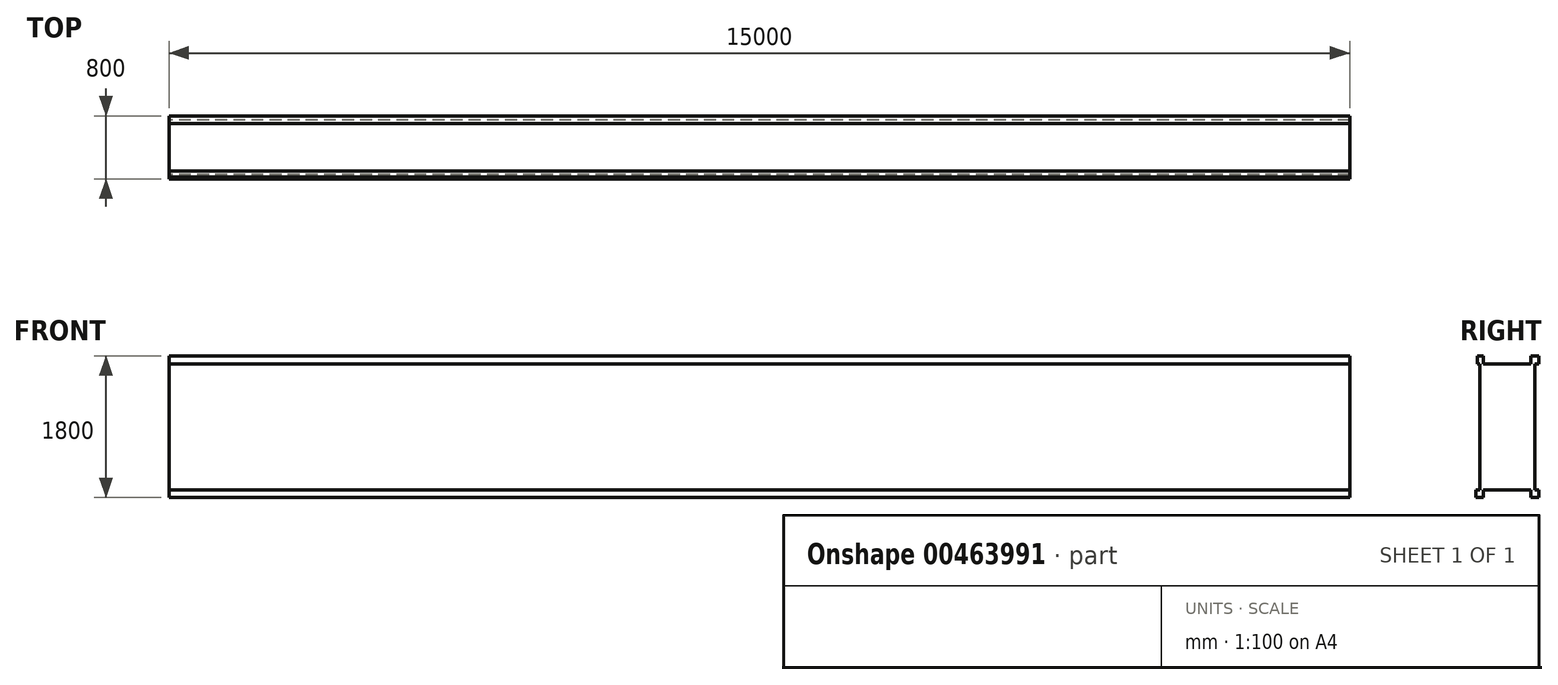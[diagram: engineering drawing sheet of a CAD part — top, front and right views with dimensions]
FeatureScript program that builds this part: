
annotation { "Feature Type Name" : "Feature", "Feature Type Description" : "" }
export const myFeature = defineFeature(function(context is Context, id is Id, definition is map)
    precondition{}
    {
        {
            var Q0;
            Q0=qCreatedBy(makeId("Right.planeOp"),FACE);
            var sketch = newSketch(context, id + "F0", { "sketchPlane" : qUnion([Q0])});
            skLineSegment(sketch, "E0", {"start": v(0, 0) * mm, "end": v(-100, 0) * mm});
            skLineSegment(sketch, "E1", {"start": v(-100, 0) * mm, "end": v(-100, 100) * mm});
            skLineSegment(sketch, "E2", {"start": v(-100, 100) * mm, "end": v(-700, 100) * mm});
            skLineSegment(sketch, "E3", {"start": v(-700, 100) * mm, "end": v(-700, 0) * mm});
            skLineSegment(sketch, "E4", {"start": v(-700, 0) * mm, "end": v(-800, 0) * mm});
            skPoint(sketch, "E5.endSnap0", {"position": v(-750, 0) * mm});
            skLineSegment(sketch, "E6", {"start": v(0, 0) * mm, "end": v(0, 100) * mm});
            skLineSegment(sketch, "E7", {"start": v(0, 100) * mm, "end": v(-50, 100) * mm});
            skLineSegment(sketch, "E8", {"start": v(-100, 1700) * mm, "end": v(-700, 1700) * mm});
            skLineSegment(sketch, "E9", {"start": v(-700, 1700) * mm, "end": v(-700, 1800) * mm});
            skLineSegment(sketch, "E10", {"start": v(-700, 1800) * mm, "end": v(-776.63, 1800) * mm});
            skLineSegment(sketch, "E11", {"start": v(-776.63, 1800) * mm, "end": v(-776.63, 1700) * mm});
            skLineSegment(sketch, "E12", {"start": v(-50, 100) * mm, "end": v(-50, 1700) * mm});
            skLineSegment(sketch, "E13", {"start": v(-50, 1700) * mm, "end": v(0, 1700) * mm});
            skLineSegment(sketch, "E14", {"start": v(0, 1700) * mm, "end": v(0, 1800) * mm});
            skLineSegment(sketch, "E15", {"start": v(0, 1800) * mm, "end": v(-100, 1800) * mm});
            skLineSegment(sketch, "E16", {"start": v(-100, 1800) * mm, "end": v(-100, 1700) * mm});
            skLineSegment(sketch, "E17", {"start": v(-800, 0) * mm, "end": v(-800, 100) * mm});
            skLineSegment(sketch, "E18", {"start": v(-776.63, 1700) * mm, "end": v(-746.63, 1700) * mm});
            skLineSegment(sketch, "E19", {"start": v(-746.63, 1700) * mm, "end": v(-746.63, 100) * mm});
            skLineSegment(sketch, "E20", {"start": v(-746.63, 100) * mm, "end": v(-800, 100) * mm});
            skSolve(sketch);
        }
        {
            var Q0;
            Q0=makeQuery(id+"F0.imprint","IMPRINT",FACE,{"disambiguationData":[TD([[makeQuery(id+"F0.imprint","IMPRINT",EDGE,{"derivedFrom":sQuery(id+"F0.wireOp",EDGE,"E0")}),-1.0]])]});
            extrude(context, id + "F1", {"entities" : qUnion([Q0]), "depth" : 15000 * mm});
        }
    });
